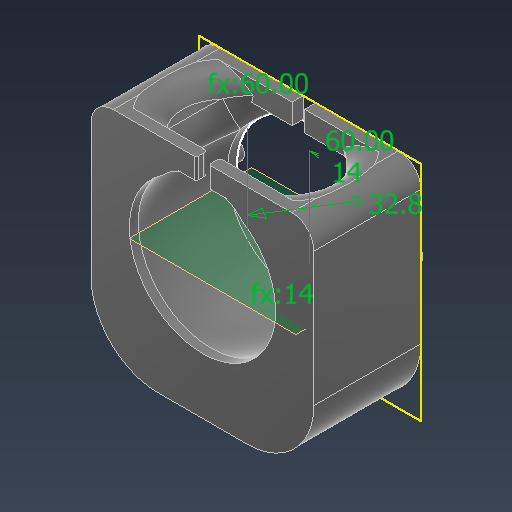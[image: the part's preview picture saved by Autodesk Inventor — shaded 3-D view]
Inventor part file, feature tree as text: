
AUTODESK INVENTOR PART (.ipt)
format: ipt  version: 2021.3 (Build 253353000, 353)  size: 502,784 bytes
history: native  units: mm
features: sketch x6, fillet x5, extrude x4, revolve x2, other x1, plane x1, hole x1, chamfer x1
ambient origin geometry x8: Origin, YZ Plane, XZ Plane, XY Plane, X Axis, Y Axis, Z Axis, Center Point
bodies: Solid1 (feature_tree)
feature tree (21):
  other  "From Stepper Mount V2"
  sketch  "Sketch2"  dims[d0=37.0mm d1=2.1mm d2=2.1mm d3=3.1mm d4=4.1mm d5=50.0mm d6=50.0mm d7=2.0mm d8=5.0mm d9=14.2mm d10=45.0deg d11=15.0mm d12=3.2mm]
  extrude  "Extrusion1"  Depth=15.0mm
  plane  "Work Plane2"
  revolve  "Revolution1"  [1 undecoded]
  hole  "Hole1"  [1 undecoded]
  fillet  "Fillet1"  Radius=3.5mm
  fillet  "Fillet2"  Radius=46.5mm
  revolve  "Revolution2"  [1 undecoded]
  fillet  "Fillet6"  Radius=0.0mm
  extrude  "Extrusion3"  Depth=3.9mm
  extrude  "Extrusion4"  Depth=20.0mm
  fillet  "Fillet9"  Radius=9.5mm
  fillet  "Fillet10"  Radius=3.085786mm
  chamfer  "Chamfer1"  Distance=25.0mm
  extrude  "Extrusion5"  Depth=20.0mm
  sketch  "Sketch5"  dims[d13=22.914214mm d14=24.085786mm]
  sketch  "Sketch6"  dims[d15=20.914214mm d16=0.0mm d17=3.5mm d18=46.5mm]
  sketch  "Sketch7"  dims[d19=3.085786mm d20=25.0mm d21=0.0mm]
  sketch  "Sketch8"  dims[d22=20.914214mm d23=3.9mm]
  sketch  "Sketch9"  dims[d24=5.5mm d25=12.414214mm d26=9.5mm d27=3.085786mm d28=25.0mm d29=44.5mm d30=46.1mm d31=20.914214mm d32=1.414214mm d33=50.0mm d34=32.8mm d35=24.0mm d36=0.0mm d40=-29.0mm d43=16.5mm d44=90.0deg d47=6.0mm d48=6.0mm d49=10.0mm d50=12.0mm d51=90.0deg d52=1.5mm d53=0.0mm d54=3.2mm d55=18.585786mm d56=9.5mm d64=2.0mm d66=20.0mm d75=15.0mm d76=5.0mm d78=60.0deg d79=60.0deg d80=2.0mm d81=2.0mm d82=10.0mm d83=90.0deg d86=14.0mm d87=14.0mm d88=10.0mm d98=4.6mm d99=0.0mm d100=6.0mm d101=6.0mm d102=2.5mm d103=2.8mm d104=4.6mm d105=0.0mm d106=5.3mm d107=0.8mm d108=0.4mm d109=2.0mm d110=45.0deg d114=3.8mm d115=23.0mm d116=24.8mm d117=12.4mm d118=3.0mm d119=0.0mm d120=4.8mm d121=4.8mm d122=4.8mm d123=10.0mm d124=10.0mm d125=2.0mm d126=2.0mm d127=20.0mm]
note: 3 required parameter values undecoded (feature->parameter linkage not recoverable at this tier; creation-order binding heuristic only, values carry confidence <= 0.55)